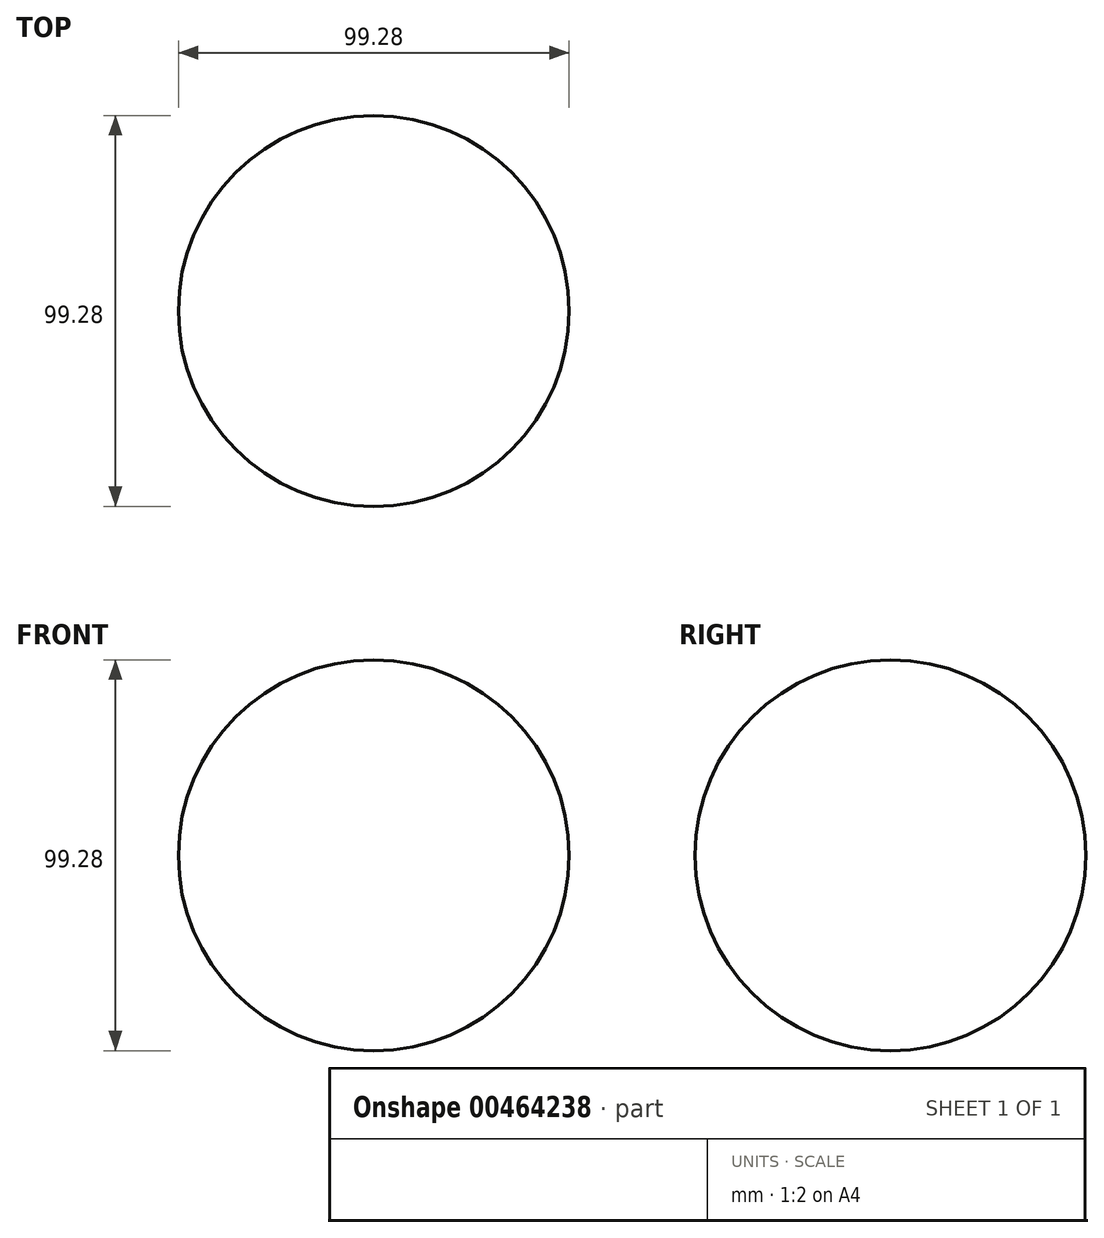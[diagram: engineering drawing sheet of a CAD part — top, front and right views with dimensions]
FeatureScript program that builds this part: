
annotation { "Feature Type Name" : "Feature", "Feature Type Description" : "" }
export const myFeature = defineFeature(function(context is Context, id is Id, definition is map)
    precondition{}
    {
        {
            var Q0;
            Q0=qCreatedBy(makeId("Top.planeOp"),FACE);
            var sketch = newSketch(context, id + "F0", { "sketchPlane" : qUnion([Q0])});
            skArc(sketch, "E0", {"start": v(0, 49.64) * mm, "mid": v(-49.64, 0) * mm, "end": v(0, -49.64) * mm});
            skLineSegment(sketch, "E1", {"start": v(0, -49.64) * mm, "end": v(0, 49.64) * mm});
            skSolve(sketch);
        }
        {
            var Q0;
            Q0=makeQuery(id+"F0.imprint","IMPRINT",FACE,{"disambiguationData":[TD([[makeQuery(id+"F0.imprint","IMPRINT",EDGE,{"derivedFrom":sQuery(id+"F0.wireOp",EDGE,"E0")}),1.0]])]});
            var Q1;
            Q1=sQuery(id+"F0.wireOp",EDGE,"E1");
            revolve(context, id + "F1", {"entities" : qUnion([Q0]), "axis" : qUnion([Q1]), "revolveType" : RevolveType.FULL});
        }
    });
